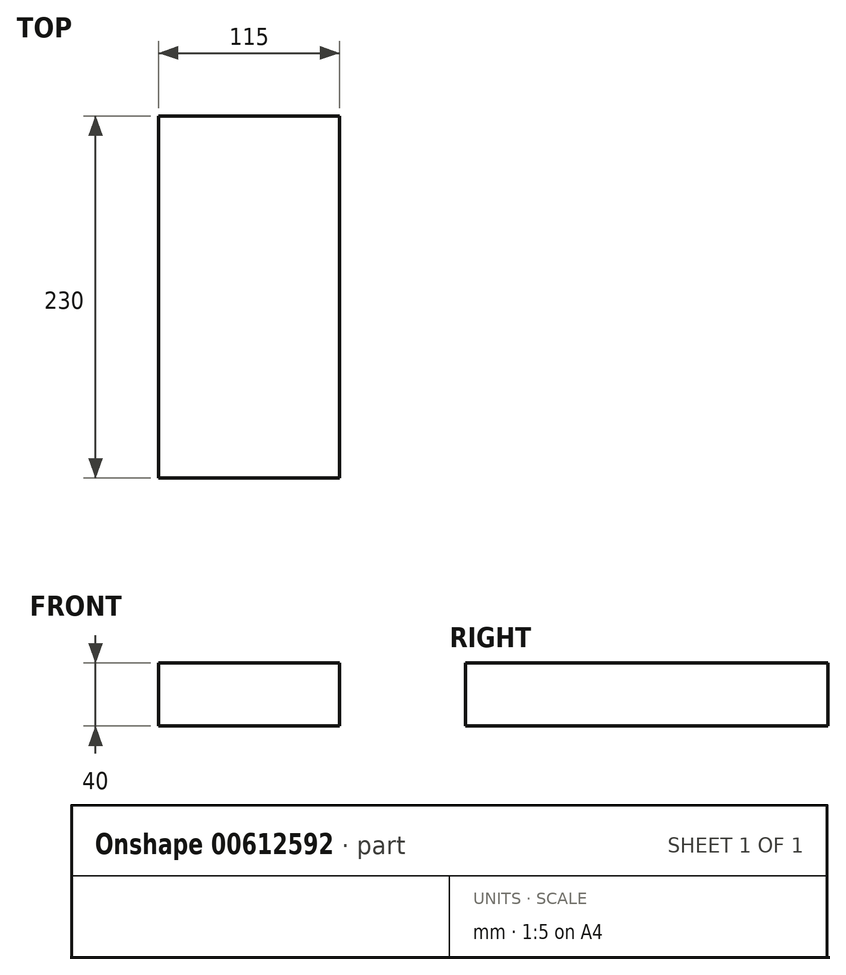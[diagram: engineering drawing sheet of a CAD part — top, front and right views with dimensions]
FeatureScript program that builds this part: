
annotation { "Feature Type Name" : "Feature", "Feature Type Description" : "" }
export const myFeature = defineFeature(function(context is Context, id is Id, definition is map)
    precondition{}
    {
        {
            var Q0;
            Q0=qCreatedBy(makeId("Front.planeOp"),FACE);
            var sketch = newSketch(context, id + "F0", { "sketchPlane" : qUnion([Q0])});
            skLineSegment(sketch, "E0.bottom", {"start": v(0, 0) * mm, "end": v(115, 0) * mm});
            skLineSegment(sketch, "E0.top", {"start": v(0, 40) * mm, "end": v(115, 40) * mm});
            skLineSegment(sketch, "E0.left", {"start": v(0, 0) * mm, "end": v(0, 40) * mm});
            skLineSegment(sketch, "E0.right", {"start": v(115, 0) * mm, "end": v(115, 40) * mm});
            skSolve(sketch);
        }
        {
            var Q0;
            Q0=makeQuery(id+"F0.imprint","IMPRINT",FACE,{"disambiguationData":[TD([[makeQuery(id+"F0.imprint","IMPRINT",EDGE,{"derivedFrom":sQuery(id+"F0.wireOp",EDGE,"E0.bottom")}),1.0]])]});
            extrude(context, id + "F1", {"entities" : qUnion([Q0]), "depth" : 230 * mm, "offsetDistance" : 25.4 * mm});
        }
    });
